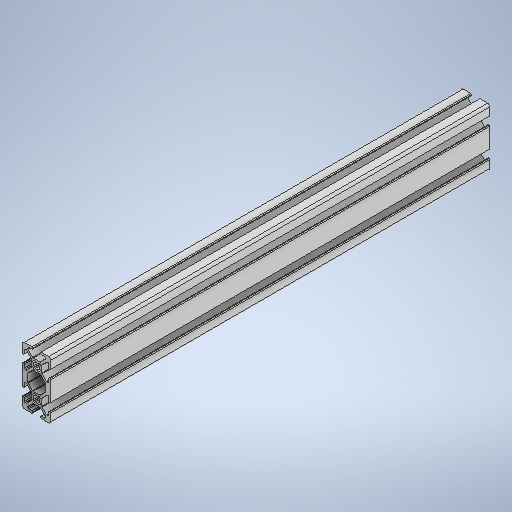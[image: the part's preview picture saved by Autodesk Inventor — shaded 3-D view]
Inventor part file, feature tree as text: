
AUTODESK INVENTOR PART (.ipt)
format: ipt  version: 2025 (Build 290162000, 162)  size: 485,376 bytes
history: native  units: in
note: dims shown in document units (in); Inventor stores cm internally (conversion verified against a paired STEP export)
features: extrude x1, sketch x1
ambient origin geometry x8: Origin, YZ Plane, XZ Plane, XY Plane, X Axis, Y Axis, Z Axis, Center Point
bodies: Solid1 (feature_tree)
feature tree (2):
  extrude  "Extrusion1"  [1 undecoded]
  sketch  "Sketch1"  dims[d0=12.0in d1=0.0in]
note: 1 required parameter value undecoded (feature->parameter linkage not recoverable at this tier; creation-order binding heuristic only, values carry confidence <= 0.55)
